# Revit family: 205_SIBOL-50-_-900
name_source: partatom
category: Duct Accessories
units: mm (PartAtom-declared; Revit-internal decimal feet)

## family parameters
Always vertical = Yes
Cut with Voids When Loaded = No
Part Type = Breaks Into
Round Connector Dimension = Use Diameter
Shared = No
Work Plane-Based = No

## types (16) — shared parameters
Description = CIRCULAR SILENCER WITH CORE
L1 = 8 mm  [stored 0.0262467 ft]
L2 = 884 mm
L2D = 900 mm
LL = 450 mm  [stored 1.47638 ft]
Manufacturer = Alnor
QmdConnectorList = 201;D;202;D
URL = http://www.ventilation-alnor.co.uk
magiPartTypeId = 205
magiProductFamilyId = SIBOL-50-*-900

## per-type parameters (varying)
| type | CD1 | CD2 | D | H2D | R | W2D |
| SIBOL-50-200-900 | 150 mm  [stored 0.492126 ft] | 151 mm  [stored 0.495407 ft] | 200 mm | 300 mm  [stored 0.984252 ft] | 100 mm  [stored 0.328084 ft] | 300 mm  [stored 0.984252 ft] |
| SIBOL-50-1000-900 | 560 mm | 561 mm | 1000 mm | 1100 mm | 500 mm | 1100 mm |
| SIBOL-50-800-900 | 450 mm  [stored 1.47638 ft] | 451 mm | 800 mm | 900 mm | 400 mm | 900 mm |
| SIBOL-50-710-900 | 400 mm | 401 mm | 710 mm | 810 mm | 355 mm | 810 mm |
| SIBOL-50-630-900 | 355 mm | 356 mm | 630 mm | 730 mm | 315 mm | 730 mm |
| SIBOL-50-600-900 | 355 mm | 356 mm | 600 mm | 700 mm | 300 mm  [stored 0.984252 ft] | 700 mm |
| SIBOL-50-560-900 | 315 mm | 316 mm | 560 mm | 660 mm | 280 mm | 660 mm |
| SIBOL-50-500-900 | 300 mm  [stored 0.984252 ft] | 301 mm | 500 mm | 600 mm | 250 mm  [stored 0.82021 ft] | 600 mm |
| SIBOL-50-450-900 | 280 mm | 281 mm | 450 mm | 550 mm | 225 mm  [stored 0.738189 ft] | 550 mm |
| SIBOL-50-400-900 | 250 mm  [stored 0.82021 ft] | 251 mm  [stored 0.823491 ft] | 400 mm | 500 mm | 200 mm  [stored 0.656168 ft] | 500 mm |
| SIBOL-50-355-900 | 200 mm  [stored 0.656168 ft] | 201 mm | 355 mm | 455 mm | 178 mm | 455 mm |
| SIBOL-50-315-900 | 200 mm  [stored 0.656168 ft] | 201 mm | 315 mm | 415 mm | 158 mm | 415 mm |
| SIBOL-50-900-900 | 500 mm | 501 mm | 900 mm | 1000 mm | 450 mm  [stored 1.47638 ft] | 1000 mm |
| SIBOL-50-280-900 | 200 mm  [stored 0.656168 ft] | 201 mm | 280 mm | 380 mm | 140 mm | 380 mm |
| SIBOL-50-250-900 | 178 mm | 179 mm | 250 mm | 350 mm | 125 mm | 350 mm |
| SIBOL-50-224-900 | 158 mm | 159 mm | 224 mm | 324 mm | 112 mm | 324 mm |

note: column(s) folded — value = type name in every type: MC Product Code, magiProductId

note: [stored X ft] marks values corroborated as IEEE doubles in the binary element streams (Revit-internal decimal feet)

## geometry (parser evidence)
native form markers: Blend x4, Sweep x1
no freeform markers — native parametric forms only
